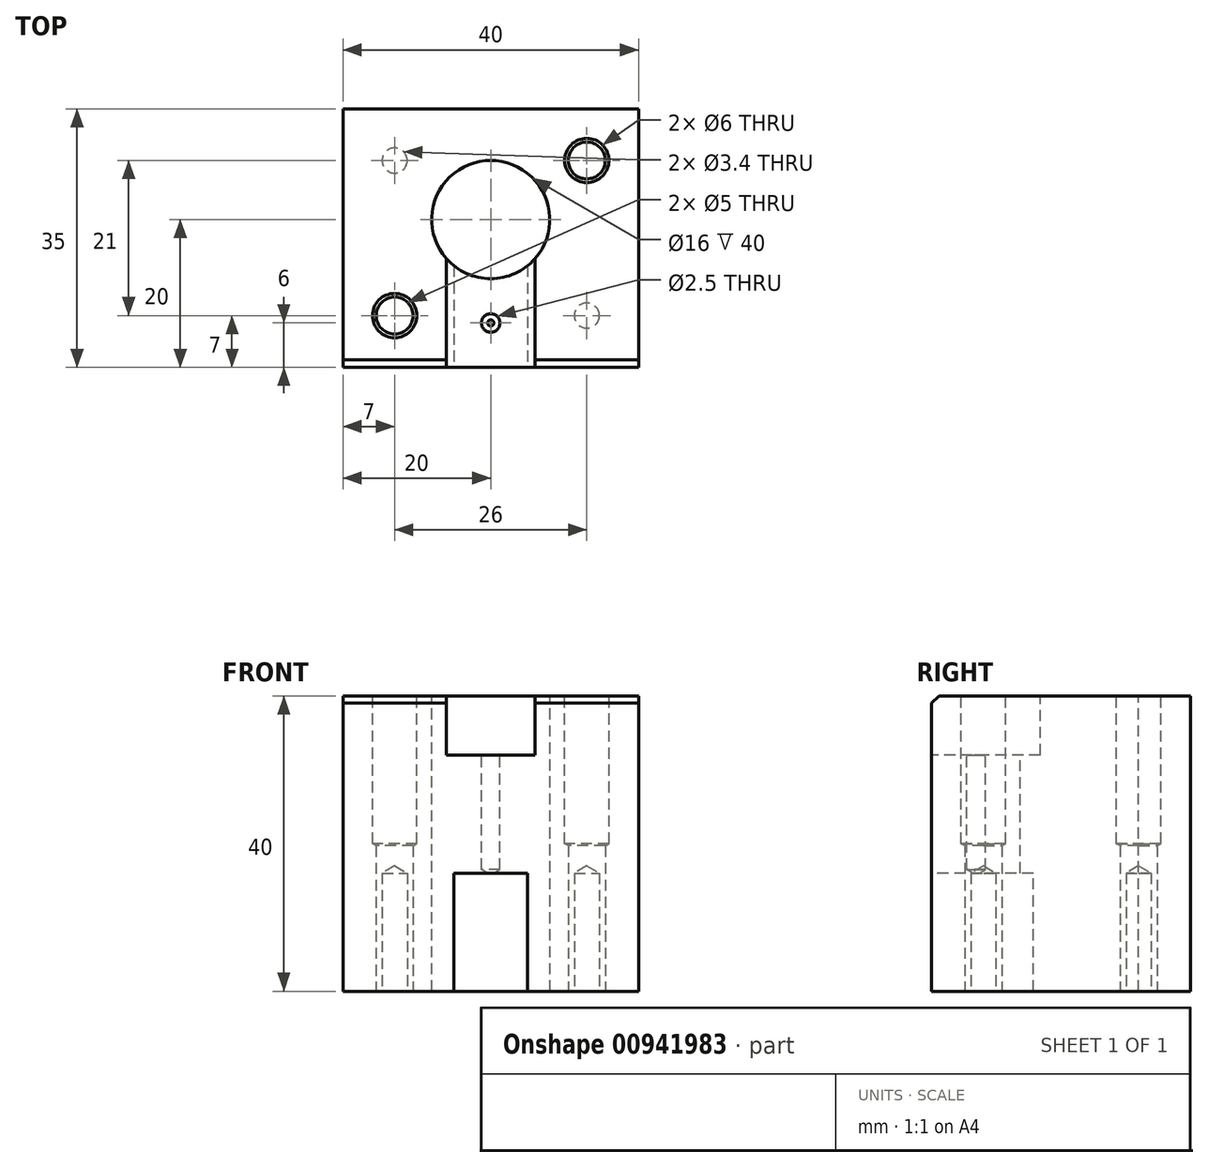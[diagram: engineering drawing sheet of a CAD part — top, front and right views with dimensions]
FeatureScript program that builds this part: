
annotation { "Feature Type Name" : "Feature", "Feature Type Description" : "" }
export const myFeature = defineFeature(function(context is Context, id is Id, definition is map)
    precondition{}
    {
        {
            var Q0;
            Q0=qCreatedBy(makeId("Top.planeOp"),FACE);
            var sketch = newSketch(context, id + "F0", { "sketchPlane" : qUnion([Q0])});
            skLineSegment(sketch, "E0.bottom", {"start": v(20, -17.5) * mm, "end": v(-20, -17.5) * mm});
            skLineSegment(sketch, "E0.top", {"start": v(20, 17.5) * mm, "end": v(-20, 17.5) * mm});
            skLineSegment(sketch, "E0.left", {"start": v(20, -17.5) * mm, "end": v(20, 17.5) * mm});
            skLineSegment(sketch, "E0.right", {"start": v(-20, -17.5) * mm, "end": v(-20, 17.5) * mm});
            skPoint(sketch, "E0.middle", {"position": v(0, 0) * mm});
            skSolve(sketch);
        }
        {
            var Q0;
            Q0=makeQuery(id+"F0.imprint","IMPRINT",FACE,{"disambiguationData":[TD([[makeQuery(id+"F0.imprint","IMPRINT",EDGE,{"derivedFrom":sQuery(id+"F0.wireOp",EDGE,"E0.bottom")}),-1.0]])]});
            extrude(context, id + "F1", {"entities" : qUnion([Q0]), "depth" : 40 * mm, "offsetDistance" : 25 * mm});
        }
        {
            var Q0;
            Q0=makeQuery(id+"F1.opExtrude","CAP_EDGE",EDGE,{"disambiguationData":[OSD([sQuery(id+"F0.wireOp",EDGE,"E0.bottom")])],"isStart":false});
            chamfer(context, id + "F2", {"entities" : qUnion([Q0]), "width" : 1 * mm, "tangentPropagation" : true});
        }
        {
            var Q0;
            Q0=makeQuery(id+"F1.opExtrude","CAP_FACE",FACE,{"disambiguationData":[OSD([sQuery(id+"F0.wireOp",EDGE,"E0.bottom"),sQuery(id+"F0.wireOp",EDGE,"E0.top"),sQuery(id+"F0.wireOp",EDGE,"E0.left"),sQuery(id+"F0.wireOp",EDGE,"E0.right")])],"isStart":false});
            var sketch = newSketch(context, id + "F3", { "sketchPlane" : qUnion([Q0])});
            skSolve(sketch);
        }
        {
            var Q0;
            {var subQ0=sQuery(id+"F0.wireOp",EDGE,"E0.top");Q0=makeQuery(id+"F3.imprint","IMPRINT",FACE,{"disambiguationData":[TD([[makeQuery(id+"F3.imprint","IMPRINT",EDGE,{"derivedFrom":makeQuery(id+"F1.opExtrude","CAP_EDGE",EDGE,{"disambiguationData":[OSD([subQ0])],"isStart":false})}),1.0]])]});}
            var sketch = newSketch(context, id + "F4", { "sketchPlane" : qUnion([Q0])});
            skPoint(sketch, "E1", {"position": v(0, 2.5) * mm});
            skSolve(sketch);
        }
        {
            var Q0;
            Q0=sQuery(id+"F4.wireOp",VERTEX,"E1");
            var Q1;
            Q1=makeQuery(id+"F1.opExtrude","SWEPT_BODY",BODY,{"disambiguationData":[OSD([sQuery(id+"F0.wireOp",EDGE,"E0.bottom"),sQuery(id+"F0.wireOp",EDGE,"E0.top"),sQuery(id+"F0.wireOp",EDGE,"E0.left"),sQuery(id+"F0.wireOp",EDGE,"E0.right")])]});
            hole(context, id + "F5", {"style" : HoleStyle.SIMPLE, "endStyle" : HoleEndStyle.THROUGH, "holeDiameter" : 16 * mm, "majorDiameter" : 4 * mm, "isTappedThrough" : true, "tappedDepth" : 12 * mm, "tapClearance" : 3, "startFromSketch" : true, "locations" : qUnion([Q0]), "scope" : qUnion([Q1])});
        }
        {
            var Q0;
            Q0=makeQuery(id+"F1.opExtrude","SWEPT_FACE",FACE,{"disambiguationData":[OSD([sQuery(id+"F0.wireOp",EDGE,"E0.bottom")])]});
            var sketch = newSketch(context, id + "F6", { "sketchPlane" : qUnion([Q0])});
            skLineSegment(sketch, "E2.bottom", {"start": v(6, 40) * mm, "end": v(-6, 40) * mm});
            skLineSegment(sketch, "E2.top", {"start": v(6, 32) * mm, "end": v(-6, 32) * mm});
            skLineSegment(sketch, "E2.left", {"start": v(6, 40) * mm, "end": v(6, 32) * mm});
            skLineSegment(sketch, "E2.right", {"start": v(-6, 40) * mm, "end": v(-6, 32) * mm});
            skPoint(sketch, "E2.middle", {"position": v(0, 36) * mm});
            skPoint(sketch, "E2.middle.positionSnap0", {"position": v(0, 39) * mm});
            skPoint(sketch, "E2.centerSnap0", {"position": v(0, 39) * mm});
            skSolve(sketch);
        }
        {
            var Q0;
            Q0 = qSketchRegion(id + "F6", true);
            extrude(context, id + "F7", {"entities" : qUnion([Q0]), "operationType" : NewBodyOperationType.REMOVE, "oppositeDirection" : true, "depth" : 25 * mm, "offsetDistance" : 25 * mm});
        }
        {
            var Q0;
            Q0=makeQuery(id+"F1.opExtrude","SWEPT_FACE",FACE,{"disambiguationData":[OSD([sQuery(id+"F0.wireOp",EDGE,"E0.bottom")])]});
            var sketch = newSketch(context, id + "F8", { "sketchPlane" : qUnion([Q0])});
            skLineSegment(sketch, "E3.bottom", {"start": v(5, 0) * mm, "end": v(-5, 0) * mm});
            skLineSegment(sketch, "E3.top", {"start": v(5, 16) * mm, "end": v(-5, 16) * mm});
            skLineSegment(sketch, "E3.left", {"start": v(5, 0) * mm, "end": v(5, 16) * mm});
            skLineSegment(sketch, "E3.right", {"start": v(-5, 0) * mm, "end": v(-5, 16) * mm});
            skPoint(sketch, "E3.middle", {"position": v(0, 8) * mm});
            skSolve(sketch);
        }
        {
            var Q0;
            Q0 = qSketchRegion(id + "F8", true);
            extrude(context, id + "F9", {"entities" : qUnion([Q0]), "operationType" : NewBodyOperationType.REMOVE, "endBound" : BoundingType.UP_TO_NEXT, "oppositeDirection" : true, "depth" : 25 * mm, "offsetDistance" : 25 * mm});
        }
        {
            var Q0;
            {var subQ0=sQuery(id+"F0.wireOp",EDGE,"E0.top");Q0=makeQuery(id+"F3.imprint","IMPRINT",FACE,{"disambiguationData":[TD([[makeQuery(id+"F3.imprint","IMPRINT",EDGE,{"derivedFrom":makeQuery(id+"F1.opExtrude","CAP_EDGE",EDGE,{"disambiguationData":[OSD([subQ0])],"isStart":false})}),1.0]])]});}
            var sketch = newSketch(context, id + "F10", { "sketchPlane" : qUnion([Q0])});
            skPoint(sketch, "E4", {"position": v(-13, -10.5) * mm});
            skPoint(sketch, "E5", {"position": v(13, 10.5) * mm});
            skLineSegment(sketch, "E6", {"start": v(0, 0) * mm, "end": v(0, 21.08) * mm, "construction": true});
            skSolve(sketch);
        }
        {
            var Q0;
            Q0=sQuery(id+"F10.wireOp",VERTEX,"E5");
            var Q1;
            Q1=sQuery(id+"F10.wireOp",VERTEX,"E4");
            var Q2;
            Q2=makeQuery(id+"F1.opExtrude","SWEPT_BODY",BODY,{"disambiguationData":[OSD([sQuery(id+"F0.wireOp",EDGE,"E0.bottom"),sQuery(id+"F0.wireOp",EDGE,"E0.top"),sQuery(id+"F0.wireOp",EDGE,"E0.left"),sQuery(id+"F0.wireOp",EDGE,"E0.right")])]});
            hole(context, id + "F11", {"style" : HoleStyle.SIMPLE, "endStyle" : HoleEndStyle.BLIND, "holeDiameter" : 6 * mm, "majorDiameter" : 5 * mm, "holeDepth" : 20 * mm, "isTappedThrough" : true, "tappedDepth" : 12 * mm, "tapClearance" : 3, "startFromSketch" : true, "locations" : qUnion([Q0, Q1]), "scope" : qUnion([Q2])});
        }
        {
            var Q0;
            Q0=makeQuery(id+"F1.opExtrude","CAP_FACE",FACE,{"disambiguationData":[OSD([sQuery(id+"F0.wireOp",EDGE,"E0.bottom"),sQuery(id+"F0.wireOp",EDGE,"E0.top"),sQuery(id+"F0.wireOp",EDGE,"E0.left"),sQuery(id+"F0.wireOp",EDGE,"E0.right")])],"isStart":true});
            var sketch = newSketch(context, id + "F12", { "sketchPlane" : qUnion([Q0])});
            skPoint(sketch, "E7", {"position": v(13, 10.5) * mm});
            skPoint(sketch, "E8", {"position": v(-13, -10.5) * mm});
            skSolve(sketch);
        }
        {
            var Q0;
            Q0=sQuery(id+"F12.wireOp",VERTEX,"E8");
            var Q1;
            Q1=sQuery(id+"F12.wireOp",VERTEX,"E7");
            var Q2;
            Q2=makeQuery(id+"F1.opExtrude","SWEPT_BODY",BODY,{"disambiguationData":[OSD([sQuery(id+"F0.wireOp",EDGE,"E0.bottom"),sQuery(id+"F0.wireOp",EDGE,"E0.top"),sQuery(id+"F0.wireOp",EDGE,"E0.left"),sQuery(id+"F0.wireOp",EDGE,"E0.right")])]});
            hole(context, id + "F13", {"style" : HoleStyle.SIMPLE, "endStyle" : HoleEndStyle.BLIND, "standardTappedOrClearance" : lookupTablePath({ "fit" : "Normal", "standard" : "ISO", "size" : "M3", "type" : "Clearance" }), "standardBlindInLast" : lookupTablePath({ "fit" : "Normal", "standard" : "ISO", "engagement" : "75%", "pitch" : "0.5 mm", "size" : "M3", "type" : "Clearance & tapped" }), "holeDiameter" : 3.4 * mm, "majorDiameter" : 5 * mm, "holeDepth" : 16 * mm, "isTappedThrough" : true, "tappedDepth" : 12 * mm, "tapClearance" : 3, "startFromSketch" : true, "locations" : qUnion([Q0, Q1]), "scope" : qUnion([Q2])});
        }
        {
            var Q0;
            Q0=makeQuery(id+"F1.opExtrude","CAP_FACE",FACE,{"disambiguationData":[OSD([sQuery(id+"F0.wireOp",EDGE,"E0.bottom"),sQuery(id+"F0.wireOp",EDGE,"E0.top"),sQuery(id+"F0.wireOp",EDGE,"E0.left"),sQuery(id+"F0.wireOp",EDGE,"E0.right")])],"isStart":true});
            var sketch = newSketch(context, id + "F14", { "sketchPlane" : qUnion([Q0])});
            skPoint(sketch, "E9", {"position": v(13, -10.5) * mm});
            skPoint(sketch, "E10", {"position": v(-13, 10.5) * mm});
            skSolve(sketch);
        }
        {
            var Q0;
            Q0=sQuery(id+"F14.wireOp",VERTEX,"E10");
            var Q1;
            Q1=sQuery(id+"F14.wireOp",VERTEX,"E9");
            var Q2;
            Q2=makeQuery(id+"F1.opExtrude","SWEPT_BODY",BODY,{"disambiguationData":[OSD([sQuery(id+"F0.wireOp",EDGE,"E0.bottom"),sQuery(id+"F0.wireOp",EDGE,"E0.top"),sQuery(id+"F0.wireOp",EDGE,"E0.left"),sQuery(id+"F0.wireOp",EDGE,"E0.right")])]});
            hole(context, id + "F15", {"style" : HoleStyle.SIMPLE, "endStyle" : HoleEndStyle.BLIND, "standardTappedOrClearance" : lookupTablePath({ "standard" : "ISO", "size" : "5", "type" : "Drilled" }), "standardBlindInLast" : lookupTablePath({ "standard" : "ISO", "size" : "5", "type" : "Drilled" }), "holeDiameter" : 5 * mm, "majorDiameter" : 5 * mm, "holeDepth" : 21 * mm, "isTappedThrough" : true, "tappedDepth" : 12 * mm, "tapClearance" : 3, "startFromSketch" : true, "locations" : qUnion([Q0, Q1]), "scope" : qUnion([Q2])});
        }
        {
            var Q0;
            Q0=makeQuery(id+"F7.boolean.opBoolean","COPY",FACE,{"derivedFrom":makeQuery(id+"F7.opExtrude","SWEPT_FACE",FACE,{"disambiguationData":[OSD([sQuery(id+"F6.wireOp",EDGE,"E2.top")])]})});
            var sketch = newSketch(context, id + "F16", { "sketchPlane" : qUnion([Q0])});
            skPoint(sketch, "E11", {"position": v(0, -11.5) * mm});
            skSolve(sketch);
        }
        {
            var Q0;
            Q0=sQuery(id+"F16.wireOp",VERTEX,"E11");
            var Q1;
            Q1=makeQuery(id+"F1.opExtrude","SWEPT_BODY",BODY,{"disambiguationData":[OSD([sQuery(id+"F0.wireOp",EDGE,"E0.bottom"),sQuery(id+"F0.wireOp",EDGE,"E0.top"),sQuery(id+"F0.wireOp",EDGE,"E0.left"),sQuery(id+"F0.wireOp",EDGE,"E0.right")])]});
            hole(context, id + "F17", {"style" : HoleStyle.SIMPLE, "endStyle" : HoleEndStyle.BLIND, "standardTappedOrClearance" : lookupTablePath({ "standard" : "ISO", "engagement" : "75%", "pitch" : "0.5 mm", "size" : "M3", "type" : "Tapped" }), "standardBlindInLast" : lookupTablePath({ "standard" : "ISO", "fit" : "Normal", "engagement" : "75%", "pitch" : "0.5 mm", "size" : "M3", "type" : "Clearance & tapped" }), "holeDiameter" : 2.5 * mm, "majorDiameter" : 3 * mm, "showTappedDepth" : true, "holeDepth" : 15.5 * mm, "isTappedThrough" : true, "tappedDepth" : 14 * mm, "tapClearance" : 3, "startFromSketch" : true, "locations" : qUnion([Q0]), "scope" : qUnion([Q1])});
        }
    });
